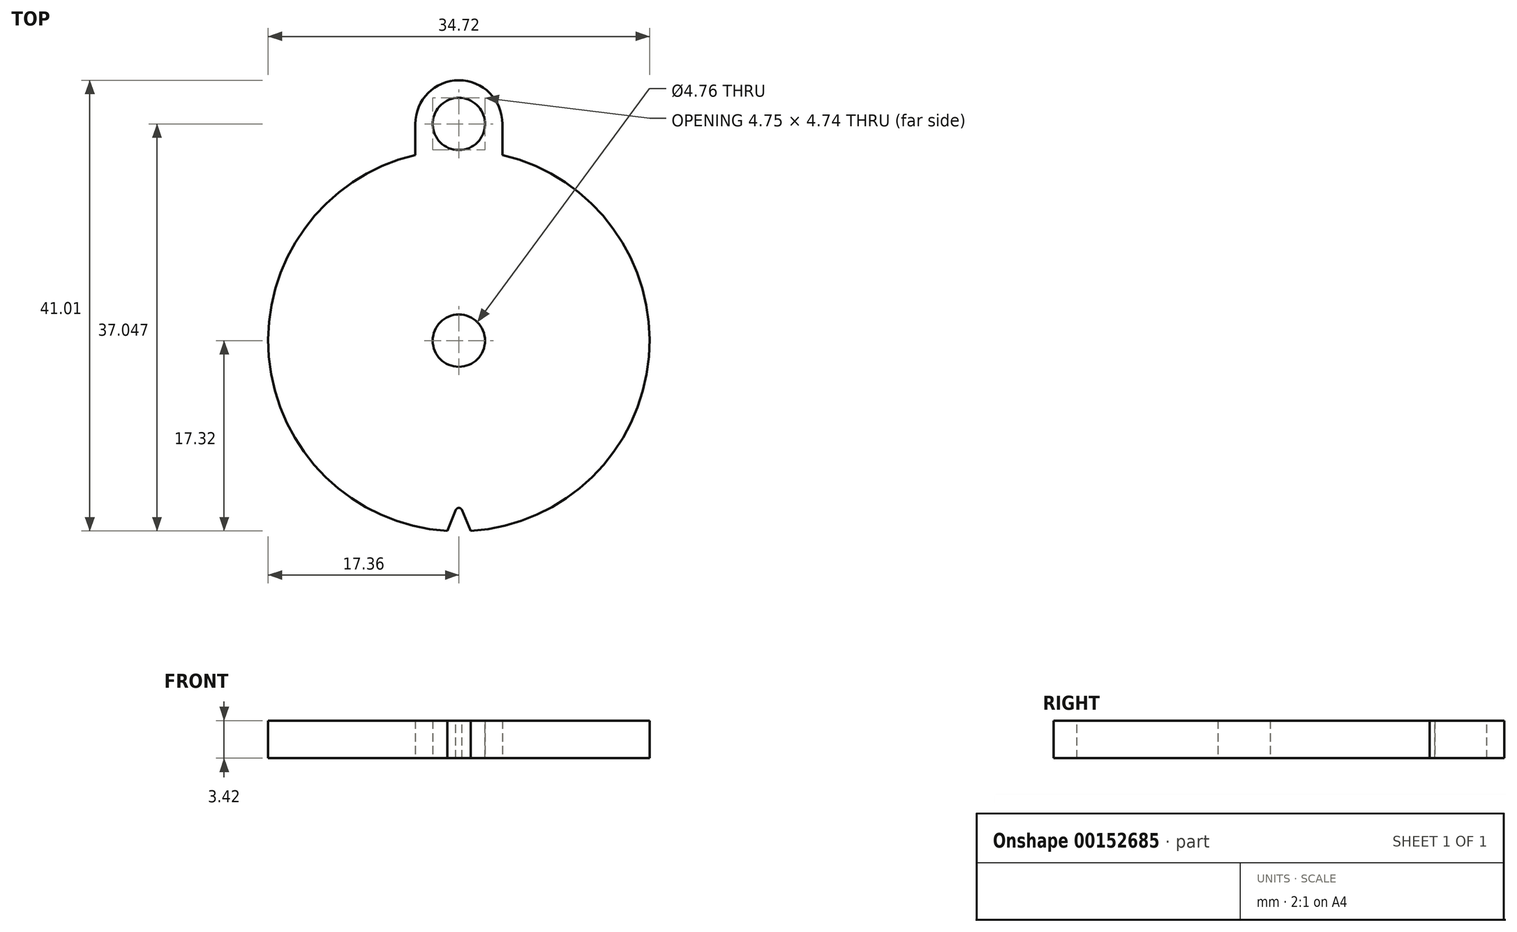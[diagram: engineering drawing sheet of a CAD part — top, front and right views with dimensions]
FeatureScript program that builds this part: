
annotation { "Feature Type Name" : "Feature", "Feature Type Description" : "" }
export const myFeature = defineFeature(function(context is Context, id is Id, definition is map)
    precondition{}
    {
        {
            var Q0;
            Q0=qCreatedBy(makeId("Top.planeOp"),FACE);
            var sketch = newSketch(context, id + "F0", { "sketchPlane" : qUnion([Q0])});
            skCircle(sketch, "E0", {"center": v(0, 0) * mm, "radius": 2.38 * mm});
            skCircle(sketch, "E1", {"center": v(0, 0) * mm, "radius": 17.36 * mm});
            skSolve(sketch);
        }
        {
            var Q0;
            Q0=qSketchRegion(id+"F0",true);
            extrude(context, id + "F1", {"entities" : qUnion([Q0]), "depth" : 3.42 * mm});
        }
        {
            var Q0;
            Q0=makeQuery(id+"F1.opExtrude","CAP_FACE",FACE,{"disambiguationData":[OSD([sQuery(id+"F0.wireOp",EDGE,"E0"),sQuery(id+"F0.wireOp",EDGE,"9VQFbyNB-fE12-b5NY-YSnJ-ty19VNcWsm2t"),sQuery(id+"F0.wireOp",EDGE,"Ty0NDWwg-i4xV-D16U-vT6m-Fo6MEusvoCE3.left"),sQuery(id+"F0.wireOp",EDGE,"Ty0NDWwg-i4xV-D16U-vT6m-Fo6MEusvoCE3.right"),sQuery(id+"F0.wireOp",EDGE,"7AfjDNlD-9QVt-SO8J-ShNI-4AUI57sHTlYq"),sQuery(id+"F0.wireOp",EDGE,"Ekzoptep-9Yjb-MUa7-IIFr-hfKKzDlXFa6H.bottom"),sQuery(id+"F0.wireOp",EDGE,"Ekzoptep-9Yjb-MUa7-IIFr-hfKKzDlXFa6H.top"),sQuery(id+"F0.wireOp",EDGE,"Ekzoptep-9Yjb-MUa7-IIFr-hfKKzDlXFa6H.left"),sQuery(id+"F0.wireOp",EDGE,"Ekzoptep-9Yjb-MUa7-IIFr-hfKKzDlXFa6H.right")])],"isStart":false});
            var sketch = newSketch(context, id + "F2", { "sketchPlane" : qUnion([Q0])});
            skLineSegment(sketch, "E2", {"start": v(0, 0) * mm, "end": v(0, -17.36) * mm, "construction": true});
            skLineSegment(sketch, "E3", {"start": v(0, 0) * mm, "end": v(0.7, -17.34) * mm, "construction": true});
            skArc(sketch, "E4", {"start": v(-1.06, -17.32) * mm, "mid": v(0, -17.36) * mm, "end": v(1.06, -17.32) * mm});
            skLineSegment(sketch, "E5", {"start": v(-1.06, -17.32) * mm, "end": v(-0.28, -15.4) * mm});
            skLineSegment(sketch, "E6", {"start": v(1.06, -17.32) * mm, "end": v(0.28, -15.4) * mm});
            skArc(sketch, "E7", {"start": v(0.28, -15.4) * mm, "mid": v(0, -15.22) * mm, "end": v(-0.28, -15.4) * mm});
            skPoint(sketch, "E8", {"position": v(0.67, -16.36) * mm});
            skSolve(sketch);
        }
        {
            var Q0;
            Q0=qSketchRegion(id+"F2",true);
            var Q1;
            Q1=makeQuery(id+"F1.opExtrude","CAP_FACE",FACE,{"disambiguationData":[OSD([sQuery(id+"F0.wireOp",EDGE,"E0"),sQuery(id+"F0.wireOp",EDGE,"9VQFbyNB-fE12-b5NY-YSnJ-ty19VNcWsm2t"),sQuery(id+"F0.wireOp",EDGE,"Ty0NDWwg-i4xV-D16U-vT6m-Fo6MEusvoCE3.left"),sQuery(id+"F0.wireOp",EDGE,"Ty0NDWwg-i4xV-D16U-vT6m-Fo6MEusvoCE3.right"),sQuery(id+"F0.wireOp",EDGE,"7AfjDNlD-9QVt-SO8J-ShNI-4AUI57sHTlYq"),sQuery(id+"F0.wireOp",EDGE,"Ekzoptep-9Yjb-MUa7-IIFr-hfKKzDlXFa6H.bottom"),sQuery(id+"F0.wireOp",EDGE,"Ekzoptep-9Yjb-MUa7-IIFr-hfKKzDlXFa6H.top"),sQuery(id+"F0.wireOp",EDGE,"Ekzoptep-9Yjb-MUa7-IIFr-hfKKzDlXFa6H.left"),sQuery(id+"F0.wireOp",EDGE,"Ekzoptep-9Yjb-MUa7-IIFr-hfKKzDlXFa6H.right")])],"isStart":true});
            extrude(context, id + "F3", {"entities" : qUnion([Q0]), "operationType" : NewBodyOperationType.REMOVE, "endBound" : BoundingType.UP_TO_SURFACE, "oppositeDirection" : true, "endBoundEntityFace" : qUnion([Q1]), "depth" : 25.4 * mm});
        }
        {
            var Q0;
            Q0=makeQuery(id+"F1.opExtrude","CAP_FACE",FACE,{"disambiguationData":[OSD([sQuery(id+"F0.wireOp",EDGE,"E0"),sQuery(id+"F0.wireOp",EDGE,"E1")])],"isStart":false});
            var sketch = newSketch(context, id + "F4", { "sketchPlane" : qUnion([Q0])});
            skLineSegment(sketch, "E9.bottom", {"start": v(-3.97, 2.38) * mm, "end": v(3.97, 2.38) * mm});
            skLineSegment(sketch, "E9.top", {"start": v(-3.97, 19.72) * mm, "end": v(3.97, 19.72) * mm, "construction": true});
            skLineSegment(sketch, "E9.left", {"start": v(-3.97, 2.38) * mm, "end": v(-3.97, 19.72) * mm});
            skLineSegment(sketch, "E9.right", {"start": v(3.97, 2.38) * mm, "end": v(3.97, 19.72) * mm});
            skLineSegment(sketch, "E10", {"start": v(0, 2.38) * mm, "end": v(0, 0) * mm, "construction": true});
            skArc(sketch, "E11", {"start": v(3.97, 19.72) * mm, "mid": v(0, 23.69) * mm, "end": v(-3.97, 19.72) * mm});
            skCircle(sketch, "E12", {"center": v(0, 19.72) * mm, "radius": 2.38 * mm});
            skSolve(sketch);
        }
        {
            var Q0;
            Q0 = qSketchRegion(id + "F4", true);
            var Q1;
            Q1=makeQuery(id+"F1.opExtrude","CAP_FACE",FACE,{"disambiguationData":[OSD([sQuery(id+"F0.wireOp",EDGE,"E0"),sQuery(id+"F0.wireOp",EDGE,"E1")])],"isStart":true});
            extrude(context, id + "F5", {"entities" : qUnion([Q0]), "operationType" : NewBodyOperationType.ADD, "endBound" : BoundingType.UP_TO_SURFACE, "oppositeDirection" : true, "endBoundEntityFace" : qUnion([Q1]), "depth" : 25.4 * mm});
        }
    });
